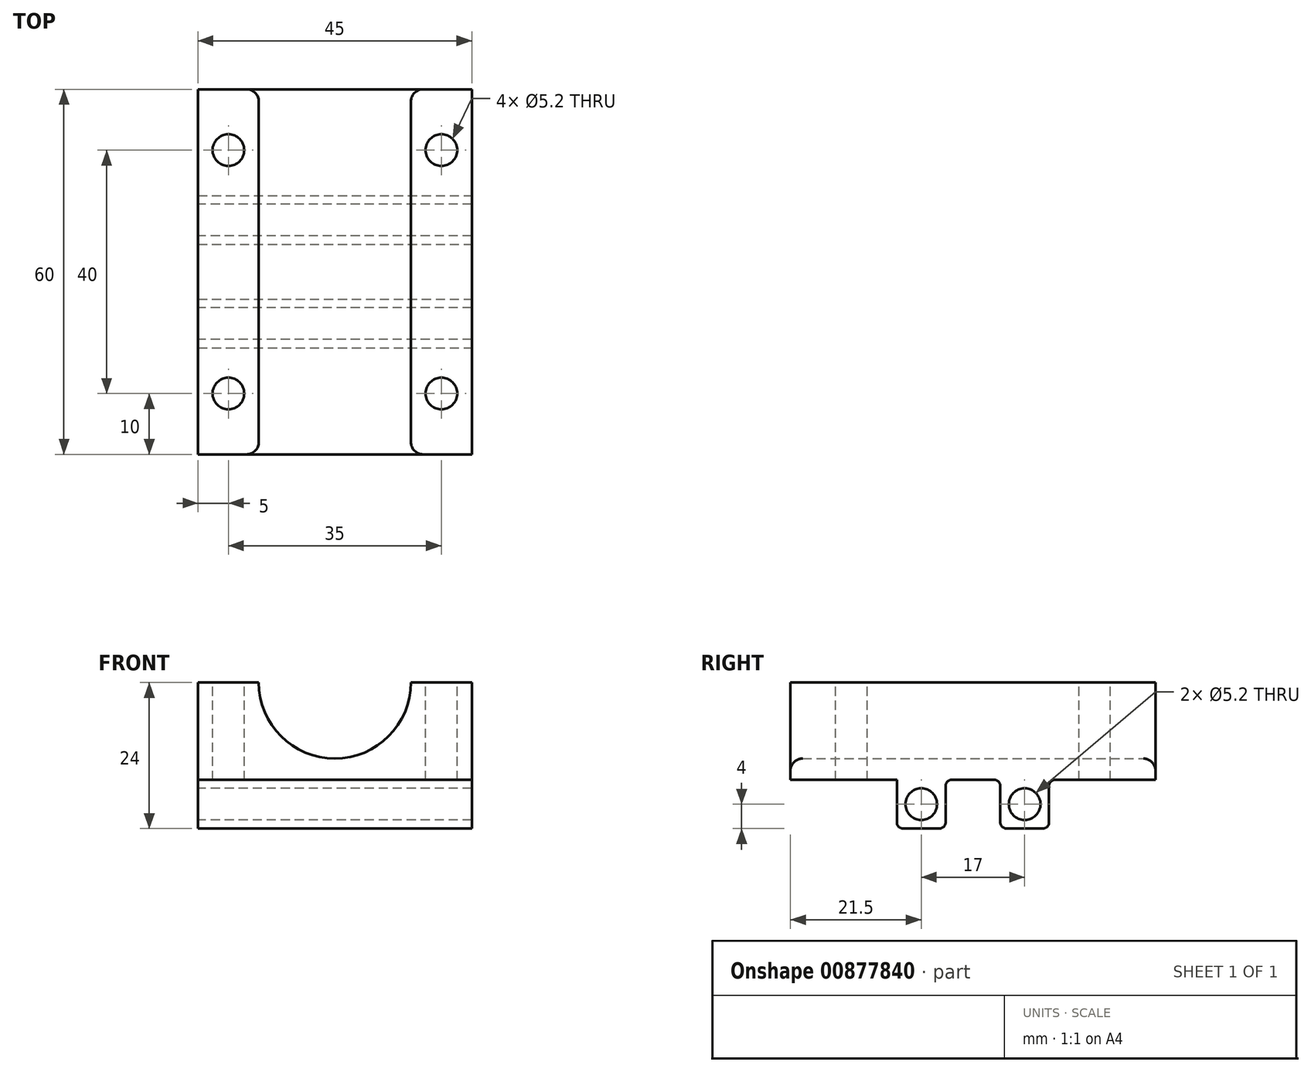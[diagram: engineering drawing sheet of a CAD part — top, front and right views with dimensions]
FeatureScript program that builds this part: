
annotation { "Feature Type Name" : "Feature", "Feature Type Description" : "" }
export const myFeature = defineFeature(function(context is Context, id is Id, definition is map)
    precondition{}
    {
        {
            var Q0;
            Q0=qCreatedBy(makeId("Front.planeOp"),FACE);
            var sketch = newSketch(context, id + "F0", { "sketchPlane" : qUnion([Q0])});
            skLineSegment(sketch, "E0", {"start": v(-12.5, 0) * mm, "end": v(-22.5, 0) * mm});
            skLineSegment(sketch, "E1", {"start": v(-22.5, 0) * mm, "end": v(-22.5, -16) * mm});
            skLineSegment(sketch, "E2", {"start": v(-22.5, -16) * mm, "end": v(22.5, -16) * mm});
            skLineSegment(sketch, "E3", {"start": v(22.5, -16) * mm, "end": v(22.5, 0) * mm});
            skLineSegment(sketch, "E4", {"start": v(22.5, 0) * mm, "end": v(12.5, 0) * mm});
            skArc(sketch, "E5", {"start": v(-12.5, 0) * mm, "mid": v(0, -12.5) * mm, "end": v(12.5, 0) * mm});
            skSolve(sketch);
        }
        {
            var Q0;
            Q0=qSketchRegion(id+"F0",true);
            extrude(context, id + "F1", {"entities" : qUnion([Q0]), "depth" : 60 * mm, "offsetDistance" : 25 * mm});
        }
        {
            var Q0;
            Q0=makeQuery(id+"F1.opExtrude","SWEPT_FACE",FACE,{"disambiguationData":[OSD([sQuery(id+"F0.wireOp",EDGE,"E0")])]});
            var sketch = newSketch(context, id + "F2", { "sketchPlane" : qUnion([Q0])});
            skCircle(sketch, "E6", {"center": v(-17.5, -50) * mm, "radius": 2.6 * mm});
            skPoint(sketch, "E6.centerSnap0", {"position": v(-17.5, -60) * mm});
            skCircle(sketch, "E7", {"center": v(-17.5, -10) * mm, "radius": 2.6 * mm});
            skCircle(sketch, "E8", {"center": v(17.5, -50) * mm, "radius": 2.6 * mm});
            skCircle(sketch, "E9", {"center": v(17.5, -10) * mm, "radius": 2.6 * mm});
            skSolve(sketch);
        }
        {
            var Q0;
            Q0=qSketchRegion(id+"F2",true);
            extrude(context, id + "F3", {"entities" : qUnion([Q0]), "operationType" : NewBodyOperationType.REMOVE, "oppositeDirection" : true, "depth" : 25 * mm, "offsetDistance" : 25 * mm});
        }
        {
            var Q0;
            Q0=makeQuery(id+"F1.opExtrude","CAP_EDGE",EDGE,{"disambiguationData":[OSD([sQuery(id+"F0.wireOp",EDGE,"E5")])],"isStart":false});
            var Q1;
            Q1=makeQuery(id+"F1.opExtrude","CAP_EDGE",EDGE,{"disambiguationData":[OSD([sQuery(id+"F0.wireOp",EDGE,"E5")])],"isStart":true});
            fillet(context, id + "F4", {"entities" : qUnion([Q0, Q1]), "radius" : 2 * mm, "tangentPropagation" : true, "allowEdgeOverflow" : false});
        }
        {
            var Q0;
            Q0=makeQuery(id+"F1.opExtrude","SWEPT_FACE",FACE,{"disambiguationData":[OSD([sQuery(id+"F0.wireOp",EDGE,"E2")])]});
            var sketch = newSketch(context, id + "F5", { "sketchPlane" : qUnion([Q0])});
            skLineSegment(sketch, "E10.bottom", {"start": v(-22.5, 17.5) * mm, "end": v(22.5, 17.5) * mm});
            skLineSegment(sketch, "E10.top", {"start": v(-22.5, 25.5) * mm, "end": v(22.5, 25.5) * mm});
            skLineSegment(sketch, "E10.left", {"start": v(-22.5, 17.5) * mm, "end": v(-22.5, 25.5) * mm});
            skLineSegment(sketch, "E10.right", {"start": v(22.5, 17.5) * mm, "end": v(22.5, 25.5) * mm});
            skLineSegment(sketch, "E11.bottom", {"start": v(-22.5, 34.5) * mm, "end": v(22.5, 34.5) * mm});
            skLineSegment(sketch, "E11.top", {"start": v(-22.5, 42.5) * mm, "end": v(22.5, 42.5) * mm});
            skLineSegment(sketch, "E11.left", {"start": v(-22.5, 34.5) * mm, "end": v(-22.5, 42.5) * mm});
            skLineSegment(sketch, "E11.right", {"start": v(22.5, 34.5) * mm, "end": v(22.5, 42.5) * mm});
            skSolve(sketch);
        }
        {
            var Q0;
            Q0 = qSketchRegion(id + "F5", true);
            extrude(context, id + "F6", {"entities" : qUnion([Q0]), "operationType" : NewBodyOperationType.ADD, "depth" : 8 * mm, "offsetDistance" : 25 * mm});
        }
        {
            var Q0;
            Q0=makeQuery(id+"F6.boolean.opBoolean","MERGE",FACE,{"derivedFrom":[makeQuery(id+"F1.opExtrude","SWEPT_FACE",FACE,{"disambiguationData":[OSD([sQuery(id+"F0.wireOp",EDGE,"E1")])]}),makeQuery(id+"F6.opExtrude","SWEPT_FACE",FACE,{"disambiguationData":[OSD([sQuery(id+"F5.wireOp",EDGE,"E10.left")])]}),makeQuery(id+"F6.opExtrude","SWEPT_FACE",FACE,{"disambiguationData":[OSD([sQuery(id+"F5.wireOp",EDGE,"E11.left")])]})]});
            var sketch = newSketch(context, id + "F7", { "sketchPlane" : qUnion([Q0])});
            skCircle(sketch, "E12", {"center": v(38.5, -20) * mm, "radius": 2.6 * mm});
            skPoint(sketch, "E12.centerSnap0", {"position": v(42.5, -20) * mm});
            skPoint(sketch, "E12.centerSnap1", {"position": v(38.5, -24) * mm});
            skCircle(sketch, "E13", {"center": v(21.5, -20) * mm, "radius": 2.6 * mm});
            skPoint(sketch, "E13.centerSnap0", {"position": v(25.5, -20) * mm});
            skPoint(sketch, "E13.centerSnap1", {"position": v(21.5, -24) * mm});
            skSolve(sketch);
        }
        {
            var Q0;
            Q0 = qSketchRegion(id + "F7", true);
            extrude(context, id + "F8", {"entities" : qUnion([Q0]), "operationType" : NewBodyOperationType.REMOVE, "oppositeDirection" : true, "depth" : 50 * mm, "offsetDistance" : 25 * mm});
        }
        {
            var Q0;
            Q0=makeQuery(id+"F6.opExtrude","CAP_EDGE",EDGE,{"disambiguationData":[OSD([sQuery(id+"F5.wireOp",EDGE,"E10.bottom")])],"isStart":false});
            var Q1;
            Q1=makeQuery(id+"F6.opExtrude","CAP_EDGE",EDGE,{"disambiguationData":[OSD([sQuery(id+"F5.wireOp",EDGE,"E10.bottom")])],"isStart":true});
            var Q2;
            Q2=makeQuery(id+"F6.opExtrude","CAP_EDGE",EDGE,{"disambiguationData":[OSD([sQuery(id+"F5.wireOp",EDGE,"E10.top")])],"isStart":false});
            var Q3;
            Q3=makeQuery(id+"F6.opExtrude","CAP_EDGE",EDGE,{"disambiguationData":[OSD([sQuery(id+"F5.wireOp",EDGE,"E10.top")])],"isStart":true});
            var Q4;
            Q4=makeQuery(id+"F6.opExtrude","CAP_EDGE",EDGE,{"disambiguationData":[OSD([sQuery(id+"F5.wireOp",EDGE,"E11.bottom")])],"isStart":true});
            var Q5;
            Q5=makeQuery(id+"F6.opExtrude","CAP_EDGE",EDGE,{"disambiguationData":[OSD([sQuery(id+"F5.wireOp",EDGE,"E11.bottom")])],"isStart":false});
            var Q6;
            Q6=makeQuery(id+"F6.opExtrude","CAP_EDGE",EDGE,{"disambiguationData":[OSD([sQuery(id+"F5.wireOp",EDGE,"E11.top")])],"isStart":false});
            var Q7;
            Q7=makeQuery(id+"F6.opExtrude","CAP_EDGE",EDGE,{"disambiguationData":[OSD([sQuery(id+"F5.wireOp",EDGE,"E11.top")])],"isStart":true});
            fillet(context, id + "F9", {"entities" : qUnion([Q0, Q1, Q2, Q3, Q4, Q5, Q6, Q7]), "radius" : 1 * mm, "tangentPropagation" : true, "allowEdgeOverflow" : false});
        }
    });
